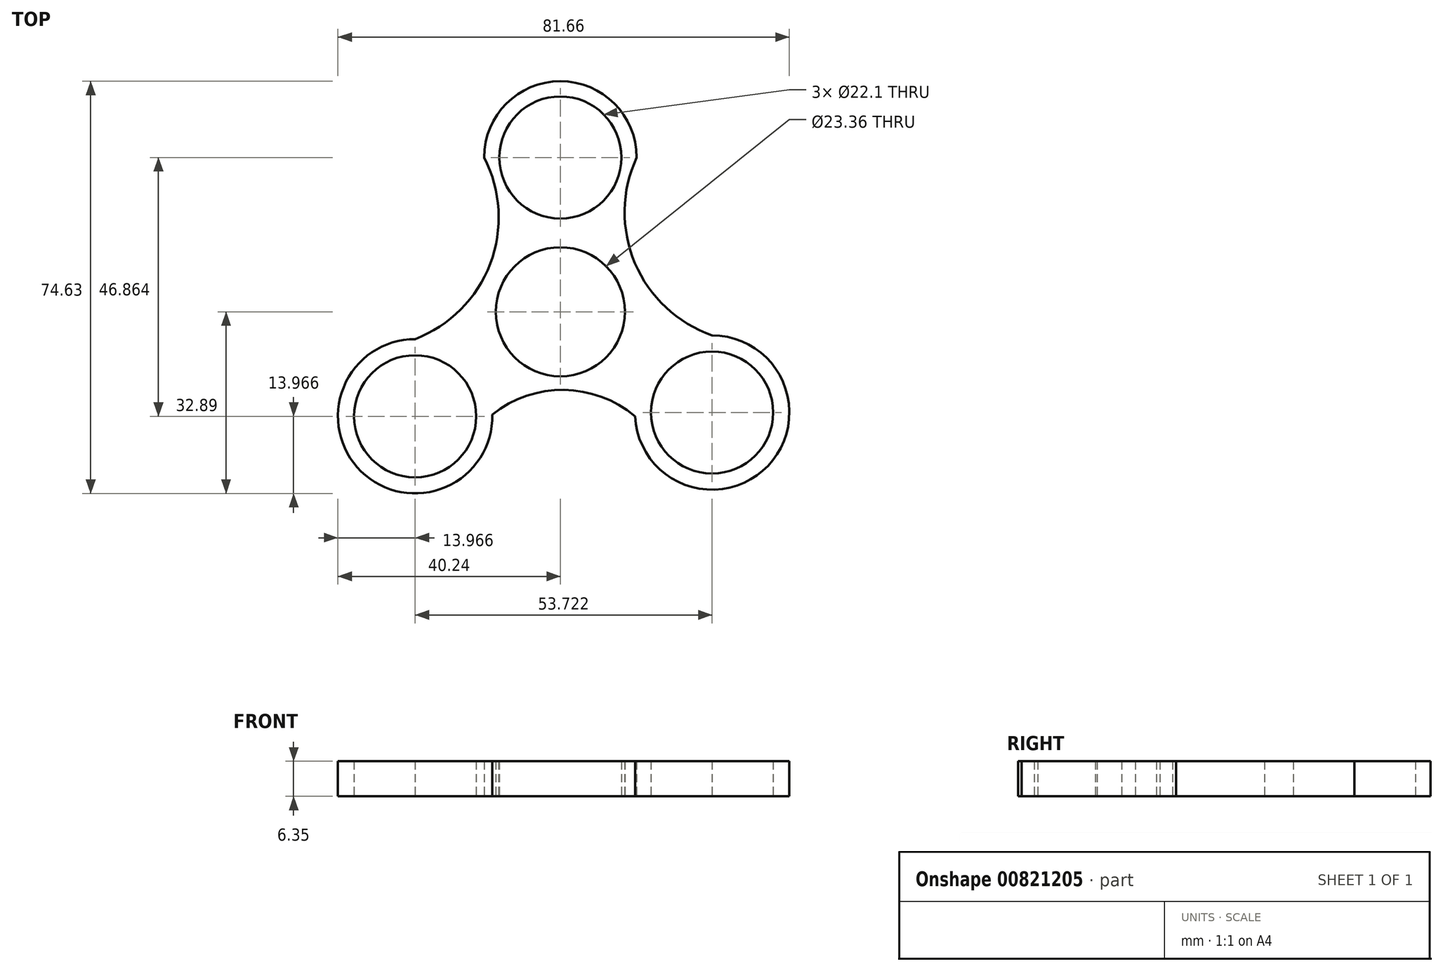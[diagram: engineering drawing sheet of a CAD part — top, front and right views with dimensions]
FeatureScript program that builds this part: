
annotation { "Feature Type Name" : "Feature", "Feature Type Description" : "" }
export const myFeature = defineFeature(function(context is Context, id is Id, definition is map)
    precondition{}
    {
        {
            var Q0;
            Q0=qCreatedBy(makeId("Top.planeOp"),FACE);
            var sketch = newSketch(context, id + "F0", { "sketchPlane" : qUnion([Q0])});
            skCircle(sketch, "E0", {"center": v(0, 0) * mm, "radius": 44.45 * mm});
            skCircle(sketch, "E1", {"center": v(0, 0) * mm, "radius": 11.68 * mm});
            skLineSegment(sketch, "E2", {"start": v(0, 0) * mm, "end": v(0, 27.94) * mm});
            skCircle(sketch, "E3", {"center": v(0, 27.94) * mm, "radius": 11.05 * mm});
            skCircle(sketch, "E4.1.0", {"center": v(-26.27, -18.92) * mm, "radius": 11.05 * mm});
            skCircle(sketch, "E4.2.0", {"center": v(27.45, -18.25) * mm, "radius": 11.05 * mm});
            skPoint(sketch, "E4.center", {"position": v(0.4, -3.08) * mm});
            skCircle(sketch, "E5", {"center": v(-26.27, -18.92) * mm, "radius": 13.97 * mm});
            skCircle(sketch, "E6", {"center": v(27.45, -18.25) * mm, "radius": 13.97 * mm});
            skCircle(sketch, "E7", {"center": v(0, 0) * mm, "radius": 13.97 * mm});
            skCircle(sketch, "E8", {"center": v(0, 27.94) * mm, "radius": 13.8 * mm});
            skArc(sketch, "E9", {"start": v(13.8, 27.94) * mm, "mid": v(13.49, 8.8) * mm, "end": v(27.45, -4.28) * mm});
            skArc(sketch, "E10", {"start": v(-26.27, -4.95) * mm, "mid": v(-12.7, 8.7) * mm, "end": v(-13.8, 27.94) * mm});
            skArc(sketch, "E11", {"start": v(13.5, -18.92) * mm, "mid": v(0.4, -14.14) * mm, "end": v(-12.7, -18.92) * mm});
            skPoint(sketch, "E11.endSnap0", {"position": v(-12.7, 8.7) * mm});
            skSolve(sketch);
        }
        {
            var Q0;
            {var subQ0=sQuery(id+"F0.wireOp",EDGE,"E5");var subQ1=sQuery(id+"F0.wireOp",EDGE,"E0");var subQ2=makeQuery(id+"F0.imprint","INTERSECT",VERTEX,{"disambiguationData":[OD(0.0)],"derivedFrom":[subQ1,subQ0]});Q0=makeQuery(id+"F0.imprint","IMPRINT",FACE,{"disambiguationData":[TD([[makeQuery(id+"F0.imprint","IMPRINT",EDGE,{"disambiguationData":[TD([[subQ2,1.0]])],"derivedFrom":subQ1}),-1.0]])]});}
            var Q1;
            {var subQ0=sQuery(id+"F0.wireOp",EDGE,"E6");var subQ1=sQuery(id+"F0.wireOp",EDGE,"E0");var subQ2=makeQuery(id+"F0.imprint","INTERSECT",VERTEX,{"disambiguationData":[OD(0.0)],"derivedFrom":[subQ1,subQ0]});Q1=makeQuery(id+"F0.imprint","IMPRINT",FACE,{"disambiguationData":[TD([[makeQuery(id+"F0.imprint","IMPRINT",EDGE,{"disambiguationData":[TD([[subQ2,-1.0]])],"derivedFrom":subQ1}),-1.0]])]});}
            var Q2;
            Q2=makeQuery(id+"F0.imprint","IMPRINT",FACE,{"disambiguationData":[TD([[makeQuery(id+"F0.imprint","IMPRINT",EDGE,{"derivedFrom":sQuery(id+"F0.wireOp",EDGE,"E4.2.0")}),-1.0]])]});
            var Q3;
            Q3=makeQuery(id+"F0.imprint","IMPRINT",FACE,{"disambiguationData":[TD([[makeQuery(id+"F0.imprint","IMPRINT",EDGE,{"derivedFrom":sQuery(id+"F0.wireOp",EDGE,"E4.1.0")}),-1.0]])]});
            var Q4;
            Q4=makeQuery(id+"F0.imprint","IMPRINT",FACE,{"disambiguationData":[TD([[makeQuery(id+"F0.imprint","IMPRINT",EDGE,{"derivedFrom":sQuery(id+"F0.wireOp",EDGE,"E7")}),-1.0]])]});
            var Q5;
            Q5=makeQuery(id+"F0.imprint","IMPRINT",FACE,{"disambiguationData":[TD([[makeQuery(id+"F0.imprint","IMPRINT",EDGE,{"derivedFrom":sQuery(id+"F0.wireOp",EDGE,"E3")}),-1.0]])]});
            var Q6;
            Q6=makeQuery(id+"F0.imprint","IMPRINT",FACE,{"disambiguationData":[TD([[makeQuery(id+"F0.imprint","IMPRINT",EDGE,{"derivedFrom":sQuery(id+"F0.wireOp",EDGE,"E1")}),-1.0]])]});
            extrude(context, id + "F1", {"entities" : qUnion([Q0, Q1, Q2, Q3, Q4, Q5, Q6]), "depth" : 6.35 * mm, "offsetDistance" : 25.4 * mm});
        }
    });
